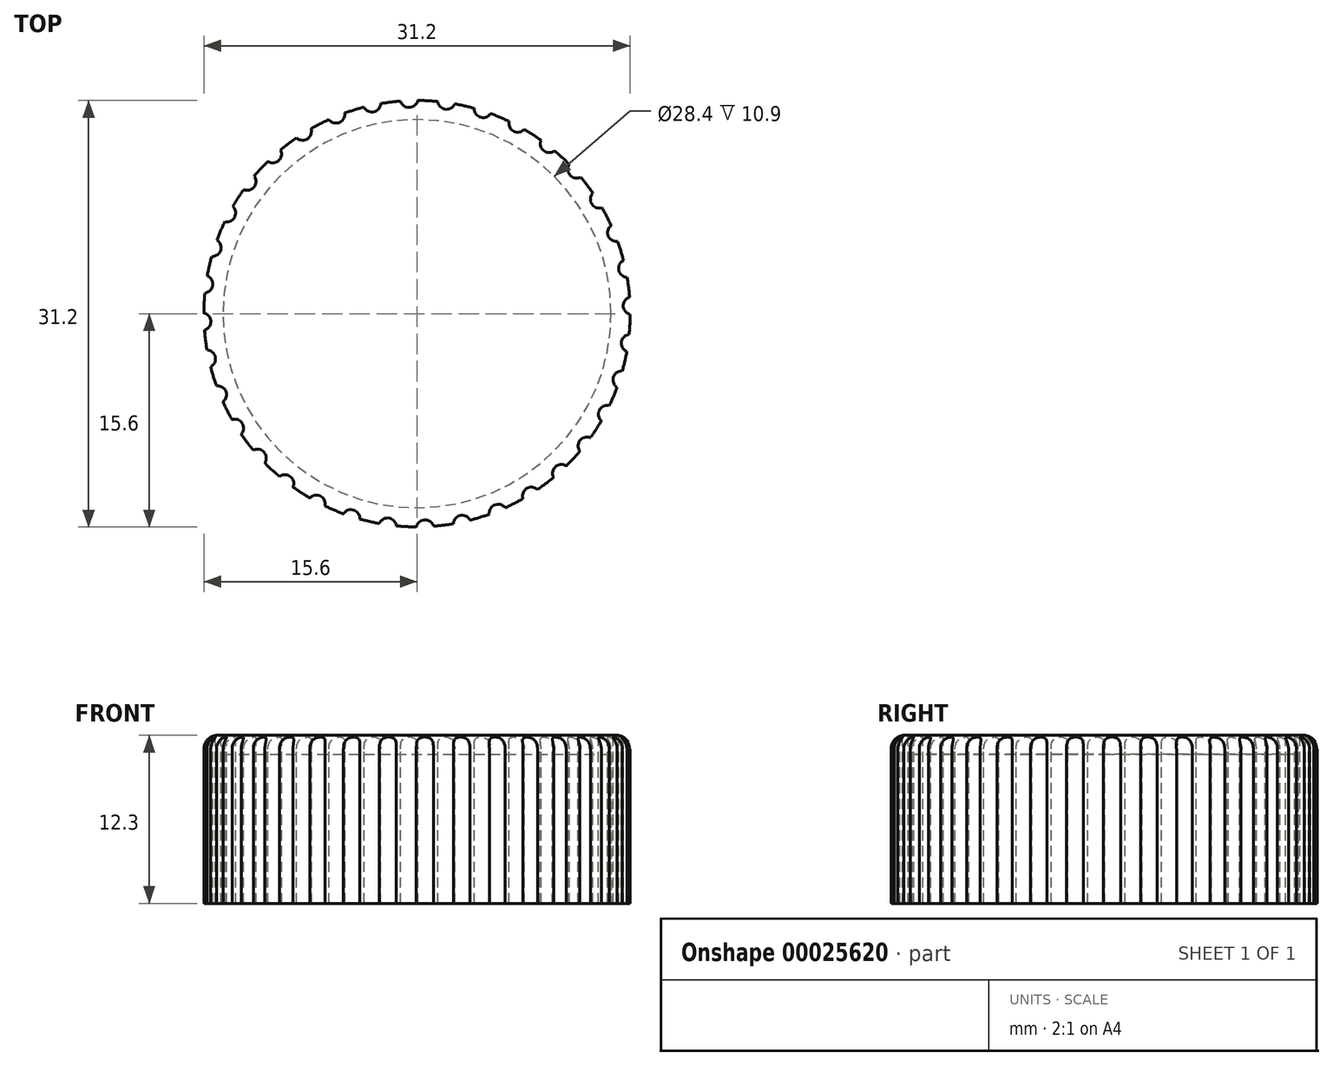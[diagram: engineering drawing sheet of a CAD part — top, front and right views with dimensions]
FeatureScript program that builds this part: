
annotation { "Feature Type Name" : "Feature", "Feature Type Description" : "" }
export const myFeature = defineFeature(function(context is Context, id is Id, definition is map)
    precondition{}
    {
        {
            var Q0;
            Q0=qCreatedBy(makeId("Front.planeOp"),FACE);
            var sketch = newSketch(context, id + "F0", { "sketchPlane" : qUnion([Q0])});
            skLineSegment(sketch, "E0", {"start": v(0, 12.3) * mm, "end": v(14.6, 12.3) * mm});
            skLineSegment(sketch, "E1", {"start": v(15.6, 11.3) * mm, "end": v(15.6, 0) * mm});
            skLineSegment(sketch, "E2.0", {"start": v(14.2, 10.9) * mm, "end": v(14.2, 0) * mm});
            skLineSegment(sketch, "E2.1", {"start": v(0, 10.9) * mm, "end": v(14.2, 10.9) * mm});
            skLineSegment(sketch, "E3", {"start": v(15.6, 0) * mm, "end": v(14.2, 0) * mm});
            skLineSegment(sketch, "E4", {"start": v(0, 10.9) * mm, "end": v(0, 12.3) * mm});
            skPoint(sketch, "E5.visualSharp", {"position": v(15.6, 12.3) * mm});
            skArc(sketch, "E5.filletArc", {"start": v(15.6, 11.3) * mm, "mid": v(15.3, 12) * mm, "end": v(14.6, 12.3) * mm});
            skSolve(sketch);
        }
        {
            var Q0;
            Q0=makeQuery(id+"F0.imprint","IMPRINT",FACE,{"disambiguationData":[TD([[makeQuery(id+"F0.imprint","IMPRINT",EDGE,{"derivedFrom":sQuery(id+"F0.wireOp",EDGE,"E0")}),-1.0]])]});
            var Q1;
            Q1=sQuery(id+"F0.wireOp",EDGE,"E4");
            revolve(context, id + "F1", {"entities" : qUnion([Q0]), "axis" : qUnion([Q1]), "revolveType" : RevolveType.FULL});
        }
        {
            var Q0;
            Q0=makeQuery(id+"F1.opRevolve","SWEPT_FACE",FACE,{"disambiguationData":[OSD([sQuery(id+"F0.wireOp",EDGE,"E0")])]});
            var sketch = newSketch(context, id + "F2", { "sketchPlane" : qUnion([Q0])});
            skCircle(sketch, "E6", {"center": v(0, 0) * mm, "radius": 15.6 * mm});
            skArc(sketch, "E7", {"start": v(-1.2, 15.55) * mm, "mid": v(-0.56, 15.09) * mm, "end": v(0.05, 15.6) * mm});
            skArc(sketch, "E8.1.0", {"start": v(-3.88, 15.1) * mm, "mid": v(-3.17, 14.76) * mm, "end": v(-2.66, 15.37) * mm});
            skArc(sketch, "E8.2.0", {"start": v(-6.45, 14.2) * mm, "mid": v(-5.69, 13.99) * mm, "end": v(-5.29, 14.68) * mm});
            skArc(sketch, "E8.3.0", {"start": v(-8.82, 12.87) * mm, "mid": v(-8.03, 12.79) * mm, "end": v(-7.76, 13.53) * mm});
            skArc(sketch, "E8.4.0", {"start": v(-10.92, 11.14) * mm, "mid": v(-10.13, 11.2) * mm, "end": v(-9.99, 11.98) * mm});
            skArc(sketch, "E8.5.0", {"start": v(-12.69, 9.08) * mm, "mid": v(-11.92, 9.27) * mm, "end": v(-11.92, 10.07) * mm});
            skArc(sketch, "E8.6.0", {"start": v(-14.07, 6.74) * mm, "mid": v(-13.35, 7.06) * mm, "end": v(-13.49, 7.84) * mm});
            skArc(sketch, "E8.7.0", {"start": v(-15.03, 4.2) * mm, "mid": v(-14.37, 4.64) * mm, "end": v(-14.64, 5.38) * mm});
            skArc(sketch, "E8.8.0", {"start": v(-15.53, 1.52) * mm, "mid": v(-14.96, 2.07) * mm, "end": v(-15.35, 2.76) * mm});
            skArc(sketch, "E8.9.0", {"start": v(-15.55, -1.2) * mm, "mid": v(-15.09, -0.56) * mm, "end": v(-15.6, 0.05) * mm});
            skArc(sketch, "E8.10.0", {"start": v(-15.1, -3.88) * mm, "mid": v(-14.76, -3.17) * mm, "end": v(-15.37, -2.66) * mm});
            skArc(sketch, "E8.11.0", {"start": v(-14.2, -6.45) * mm, "mid": v(-13.99, -5.69) * mm, "end": v(-14.68, -5.29) * mm});
            skArc(sketch, "E8.12.0", {"start": v(-12.87, -8.82) * mm, "mid": v(-12.79, -8.03) * mm, "end": v(-13.53, -7.76) * mm});
            skArc(sketch, "E8.13.0", {"start": v(-11.14, -10.92) * mm, "mid": v(-11.2, -10.13) * mm, "end": v(-11.98, -9.99) * mm});
            skArc(sketch, "E8.14.0", {"start": v(-9.08, -12.69) * mm, "mid": v(-9.27, -11.92) * mm, "end": v(-10.07, -11.92) * mm});
            skArc(sketch, "E8.15.0", {"start": v(-6.74, -14.07) * mm, "mid": v(-7.06, -13.35) * mm, "end": v(-7.84, -13.49) * mm});
            skArc(sketch, "E8.16.0", {"start": v(-4.2, -15.03) * mm, "mid": v(-4.64, -14.37) * mm, "end": v(-5.38, -14.64) * mm});
            skArc(sketch, "E8.17.0", {"start": v(-1.52, -15.53) * mm, "mid": v(-2.07, -14.96) * mm, "end": v(-2.76, -15.35) * mm});
            skArc(sketch, "E8.18.0", {"start": v(1.2, -15.55) * mm, "mid": v(0.56, -15.09) * mm, "end": v(-0.05, -15.6) * mm});
            skArc(sketch, "E8.19.0", {"start": v(3.88, -15.1) * mm, "mid": v(3.17, -14.76) * mm, "end": v(2.66, -15.37) * mm});
            skArc(sketch, "E8.20.0", {"start": v(6.45, -14.2) * mm, "mid": v(5.69, -13.99) * mm, "end": v(5.29, -14.68) * mm});
            skArc(sketch, "E8.21.0", {"start": v(8.82, -12.87) * mm, "mid": v(8.03, -12.79) * mm, "end": v(7.76, -13.53) * mm});
            skArc(sketch, "E8.22.0", {"start": v(10.92, -11.14) * mm, "mid": v(10.13, -11.2) * mm, "end": v(9.99, -11.98) * mm});
            skArc(sketch, "E8.23.0", {"start": v(12.69, -9.08) * mm, "mid": v(11.92, -9.27) * mm, "end": v(11.92, -10.07) * mm});
            skArc(sketch, "E8.24.0", {"start": v(14.07, -6.74) * mm, "mid": v(13.35, -7.06) * mm, "end": v(13.49, -7.84) * mm});
            skArc(sketch, "E8.25.0", {"start": v(15.03, -4.2) * mm, "mid": v(14.37, -4.64) * mm, "end": v(14.64, -5.38) * mm});
            skArc(sketch, "E8.26.0", {"start": v(15.53, -1.52) * mm, "mid": v(14.96, -2.07) * mm, "end": v(15.35, -2.76) * mm});
            skArc(sketch, "E8.27.0", {"start": v(15.55, 1.2) * mm, "mid": v(15.09, 0.56) * mm, "end": v(15.6, -0.05) * mm});
            skArc(sketch, "E8.28.0", {"start": v(15.1, 3.88) * mm, "mid": v(14.76, 3.17) * mm, "end": v(15.37, 2.66) * mm});
            skArc(sketch, "E8.29.0", {"start": v(14.2, 6.45) * mm, "mid": v(13.99, 5.69) * mm, "end": v(14.68, 5.29) * mm});
            skArc(sketch, "E8.30.0", {"start": v(12.87, 8.82) * mm, "mid": v(12.79, 8.03) * mm, "end": v(13.53, 7.76) * mm});
            skArc(sketch, "E8.31.0", {"start": v(11.14, 10.92) * mm, "mid": v(11.2, 10.13) * mm, "end": v(11.98, 9.99) * mm});
            skArc(sketch, "E8.32.0", {"start": v(9.08, 12.69) * mm, "mid": v(9.27, 11.92) * mm, "end": v(10.07, 11.92) * mm});
            skArc(sketch, "E8.33.0", {"start": v(6.74, 14.07) * mm, "mid": v(7.06, 13.35) * mm, "end": v(7.84, 13.49) * mm});
            skArc(sketch, "E8.34.0", {"start": v(4.2, 15.03) * mm, "mid": v(4.64, 14.37) * mm, "end": v(5.38, 14.64) * mm});
            skArc(sketch, "E8.35.0", {"start": v(1.52, 15.53) * mm, "mid": v(2.07, 14.96) * mm, "end": v(2.76, 15.35) * mm});
            skSolve(sketch);
        }
        {
            var Q0;
            {var subQ0=sQuery(id+"F2.wireOp",EDGE,"E8.32.0");Q0=makeQuery(id+"F2.imprint","IMPRINT",FACE,{"disambiguationData":[TD([[makeQuery(id+"F2.imprint","IMPRINT",EDGE,{"derivedFrom":subQ0}),1.0]])]});}
            var Q1;
            {var subQ0=sQuery(id+"F2.wireOp",EDGE,"E8.33.0");Q1=makeQuery(id+"F2.imprint","IMPRINT",FACE,{"disambiguationData":[TD([[makeQuery(id+"F2.imprint","IMPRINT",EDGE,{"derivedFrom":subQ0}),1.0]])]});}
            var Q2;
            {var subQ0=sQuery(id+"F2.wireOp",EDGE,"E8.34.0");Q2=makeQuery(id+"F2.imprint","IMPRINT",FACE,{"disambiguationData":[TD([[makeQuery(id+"F2.imprint","IMPRINT",EDGE,{"derivedFrom":subQ0}),1.0]])]});}
            var Q3;
            {var subQ0=sQuery(id+"F2.wireOp",EDGE,"E8.35.0");Q3=makeQuery(id+"F2.imprint","IMPRINT",FACE,{"disambiguationData":[TD([[makeQuery(id+"F2.imprint","IMPRINT",EDGE,{"derivedFrom":subQ0}),1.0]])]});}
            var Q4;
            {var subQ0=sQuery(id+"F2.wireOp",EDGE,"E7");Q4=makeQuery(id+"F2.imprint","IMPRINT",FACE,{"disambiguationData":[TD([[makeQuery(id+"F2.imprint","IMPRINT",EDGE,{"derivedFrom":subQ0}),1.0]])]});}
            var Q5;
            {var subQ0=sQuery(id+"F2.wireOp",EDGE,"E8.1.0");Q5=makeQuery(id+"F2.imprint","IMPRINT",FACE,{"disambiguationData":[TD([[makeQuery(id+"F2.imprint","IMPRINT",EDGE,{"derivedFrom":subQ0}),1.0]])]});}
            var Q6;
            {var subQ0=sQuery(id+"F2.wireOp",EDGE,"E8.2.0");Q6=makeQuery(id+"F2.imprint","IMPRINT",FACE,{"disambiguationData":[TD([[makeQuery(id+"F2.imprint","IMPRINT",EDGE,{"derivedFrom":subQ0}),1.0]])]});}
            var Q7;
            {var subQ0=sQuery(id+"F2.wireOp",EDGE,"E8.3.0");Q7=makeQuery(id+"F2.imprint","IMPRINT",FACE,{"disambiguationData":[TD([[makeQuery(id+"F2.imprint","IMPRINT",EDGE,{"derivedFrom":subQ0}),1.0]])]});}
            var Q8;
            {var subQ0=sQuery(id+"F2.wireOp",EDGE,"E8.4.0");Q8=makeQuery(id+"F2.imprint","IMPRINT",FACE,{"disambiguationData":[TD([[makeQuery(id+"F2.imprint","IMPRINT",EDGE,{"derivedFrom":subQ0}),1.0]])]});}
            var Q9;
            {var subQ0=sQuery(id+"F2.wireOp",EDGE,"E8.5.0");Q9=makeQuery(id+"F2.imprint","IMPRINT",FACE,{"disambiguationData":[TD([[makeQuery(id+"F2.imprint","IMPRINT",EDGE,{"derivedFrom":subQ0}),1.0]])]});}
            var Q10;
            {var subQ0=sQuery(id+"F2.wireOp",EDGE,"E8.6.0");Q10=makeQuery(id+"F2.imprint","IMPRINT",FACE,{"disambiguationData":[TD([[makeQuery(id+"F2.imprint","IMPRINT",EDGE,{"derivedFrom":subQ0}),1.0]])]});}
            var Q11;
            {var subQ0=sQuery(id+"F2.wireOp",EDGE,"E8.7.0");Q11=makeQuery(id+"F2.imprint","IMPRINT",FACE,{"disambiguationData":[TD([[makeQuery(id+"F2.imprint","IMPRINT",EDGE,{"derivedFrom":subQ0}),1.0]])]});}
            var Q12;
            {var subQ0=sQuery(id+"F2.wireOp",EDGE,"E8.8.0");Q12=makeQuery(id+"F2.imprint","IMPRINT",FACE,{"disambiguationData":[TD([[makeQuery(id+"F2.imprint","IMPRINT",EDGE,{"derivedFrom":subQ0}),1.0]])]});}
            var Q13;
            {var subQ0=sQuery(id+"F2.wireOp",EDGE,"E8.9.0");Q13=makeQuery(id+"F2.imprint","IMPRINT",FACE,{"disambiguationData":[TD([[makeQuery(id+"F2.imprint","IMPRINT",EDGE,{"derivedFrom":subQ0}),1.0]])]});}
            var Q14;
            {var subQ0=sQuery(id+"F2.wireOp",EDGE,"E8.10.0");Q14=makeQuery(id+"F2.imprint","IMPRINT",FACE,{"disambiguationData":[TD([[makeQuery(id+"F2.imprint","IMPRINT",EDGE,{"derivedFrom":subQ0}),1.0]])]});}
            var Q15;
            {var subQ0=sQuery(id+"F2.wireOp",EDGE,"E8.11.0");Q15=makeQuery(id+"F2.imprint","IMPRINT",FACE,{"disambiguationData":[TD([[makeQuery(id+"F2.imprint","IMPRINT",EDGE,{"derivedFrom":subQ0}),1.0]])]});}
            var Q16;
            {var subQ0=sQuery(id+"F2.wireOp",EDGE,"E8.12.0");Q16=makeQuery(id+"F2.imprint","IMPRINT",FACE,{"disambiguationData":[TD([[makeQuery(id+"F2.imprint","IMPRINT",EDGE,{"derivedFrom":subQ0}),1.0]])]});}
            var Q17;
            {var subQ0=sQuery(id+"F2.wireOp",EDGE,"E8.13.0");Q17=makeQuery(id+"F2.imprint","IMPRINT",FACE,{"disambiguationData":[TD([[makeQuery(id+"F2.imprint","IMPRINT",EDGE,{"derivedFrom":subQ0}),1.0]])]});}
            var Q18;
            {var subQ0=sQuery(id+"F2.wireOp",EDGE,"E8.14.0");Q18=makeQuery(id+"F2.imprint","IMPRINT",FACE,{"disambiguationData":[TD([[makeQuery(id+"F2.imprint","IMPRINT",EDGE,{"derivedFrom":subQ0}),1.0]])]});}
            var Q19;
            {var subQ0=sQuery(id+"F2.wireOp",EDGE,"E8.15.0");Q19=makeQuery(id+"F2.imprint","IMPRINT",FACE,{"disambiguationData":[TD([[makeQuery(id+"F2.imprint","IMPRINT",EDGE,{"derivedFrom":subQ0}),1.0]])]});}
            var Q20;
            {var subQ0=sQuery(id+"F2.wireOp",EDGE,"E8.16.0");Q20=makeQuery(id+"F2.imprint","IMPRINT",FACE,{"disambiguationData":[TD([[makeQuery(id+"F2.imprint","IMPRINT",EDGE,{"derivedFrom":subQ0}),1.0]])]});}
            var Q21;
            {var subQ0=sQuery(id+"F2.wireOp",EDGE,"E8.17.0");Q21=makeQuery(id+"F2.imprint","IMPRINT",FACE,{"disambiguationData":[TD([[makeQuery(id+"F2.imprint","IMPRINT",EDGE,{"derivedFrom":subQ0}),1.0]])]});}
            var Q22;
            {var subQ0=sQuery(id+"F2.wireOp",EDGE,"E8.18.0");Q22=makeQuery(id+"F2.imprint","IMPRINT",FACE,{"disambiguationData":[TD([[makeQuery(id+"F2.imprint","IMPRINT",EDGE,{"derivedFrom":subQ0}),1.0]])]});}
            var Q23;
            {var subQ0=sQuery(id+"F2.wireOp",EDGE,"E8.19.0");Q23=makeQuery(id+"F2.imprint","IMPRINT",FACE,{"disambiguationData":[TD([[makeQuery(id+"F2.imprint","IMPRINT",EDGE,{"derivedFrom":subQ0}),1.0]])]});}
            var Q24;
            {var subQ0=sQuery(id+"F2.wireOp",EDGE,"E8.31.0");Q24=makeQuery(id+"F2.imprint","IMPRINT",FACE,{"disambiguationData":[TD([[makeQuery(id+"F2.imprint","IMPRINT",EDGE,{"derivedFrom":subQ0}),1.0]])]});}
            var Q25;
            {var subQ0=sQuery(id+"F2.wireOp",EDGE,"E8.30.0");Q25=makeQuery(id+"F2.imprint","IMPRINT",FACE,{"disambiguationData":[TD([[makeQuery(id+"F2.imprint","IMPRINT",EDGE,{"derivedFrom":subQ0}),1.0]])]});}
            var Q26;
            {var subQ0=sQuery(id+"F2.wireOp",EDGE,"E8.29.0");Q26=makeQuery(id+"F2.imprint","IMPRINT",FACE,{"disambiguationData":[TD([[makeQuery(id+"F2.imprint","IMPRINT",EDGE,{"derivedFrom":subQ0}),1.0]])]});}
            var Q27;
            {var subQ0=sQuery(id+"F2.wireOp",EDGE,"E8.28.0");Q27=makeQuery(id+"F2.imprint","IMPRINT",FACE,{"disambiguationData":[TD([[makeQuery(id+"F2.imprint","IMPRINT",EDGE,{"derivedFrom":subQ0}),1.0]])]});}
            var Q28;
            {var subQ0=sQuery(id+"F2.wireOp",EDGE,"E8.27.0");Q28=makeQuery(id+"F2.imprint","IMPRINT",FACE,{"disambiguationData":[TD([[makeQuery(id+"F2.imprint","IMPRINT",EDGE,{"derivedFrom":subQ0}),1.0]])]});}
            var Q29;
            {var subQ0=sQuery(id+"F2.wireOp",EDGE,"E8.26.0");Q29=makeQuery(id+"F2.imprint","IMPRINT",FACE,{"disambiguationData":[TD([[makeQuery(id+"F2.imprint","IMPRINT",EDGE,{"derivedFrom":subQ0}),1.0]])]});}
            var Q30;
            {var subQ0=sQuery(id+"F2.wireOp",EDGE,"E8.25.0");Q30=makeQuery(id+"F2.imprint","IMPRINT",FACE,{"disambiguationData":[TD([[makeQuery(id+"F2.imprint","IMPRINT",EDGE,{"derivedFrom":subQ0}),1.0]])]});}
            var Q31;
            {var subQ0=sQuery(id+"F2.wireOp",EDGE,"E8.24.0");Q31=makeQuery(id+"F2.imprint","IMPRINT",FACE,{"disambiguationData":[TD([[makeQuery(id+"F2.imprint","IMPRINT",EDGE,{"derivedFrom":subQ0}),1.0]])]});}
            var Q32;
            {var subQ0=sQuery(id+"F2.wireOp",EDGE,"E8.23.0");Q32=makeQuery(id+"F2.imprint","IMPRINT",FACE,{"disambiguationData":[TD([[makeQuery(id+"F2.imprint","IMPRINT",EDGE,{"derivedFrom":subQ0}),1.0]])]});}
            var Q33;
            {var subQ0=sQuery(id+"F2.wireOp",EDGE,"E8.22.0");Q33=makeQuery(id+"F2.imprint","IMPRINT",FACE,{"disambiguationData":[TD([[makeQuery(id+"F2.imprint","IMPRINT",EDGE,{"derivedFrom":subQ0}),1.0]])]});}
            var Q34;
            {var subQ0=sQuery(id+"F2.wireOp",EDGE,"E8.21.0");Q34=makeQuery(id+"F2.imprint","IMPRINT",FACE,{"disambiguationData":[TD([[makeQuery(id+"F2.imprint","IMPRINT",EDGE,{"derivedFrom":subQ0}),1.0]])]});}
            var Q35;
            {var subQ0=sQuery(id+"F2.wireOp",EDGE,"E8.20.0");Q35=makeQuery(id+"F2.imprint","IMPRINT",FACE,{"disambiguationData":[TD([[makeQuery(id+"F2.imprint","IMPRINT",EDGE,{"derivedFrom":subQ0}),1.0]])]});}
            extrude(context, id + "F3", {"entities" : qUnion([Q0, Q1, Q2, Q3, Q4, Q5, Q6, Q7, Q8, Q9, Q10, Q11, Q12, Q13, Q14, Q15, Q16, Q17, Q18, Q19, Q20, Q21, Q22, Q23, Q24, Q25, Q26, Q27, Q28, Q29, Q30, Q31, Q32, Q33, Q34, Q35]), "operationType" : NewBodyOperationType.REMOVE, "oppositeDirection" : true, "depth" : 25 * mm});
        }
    });
